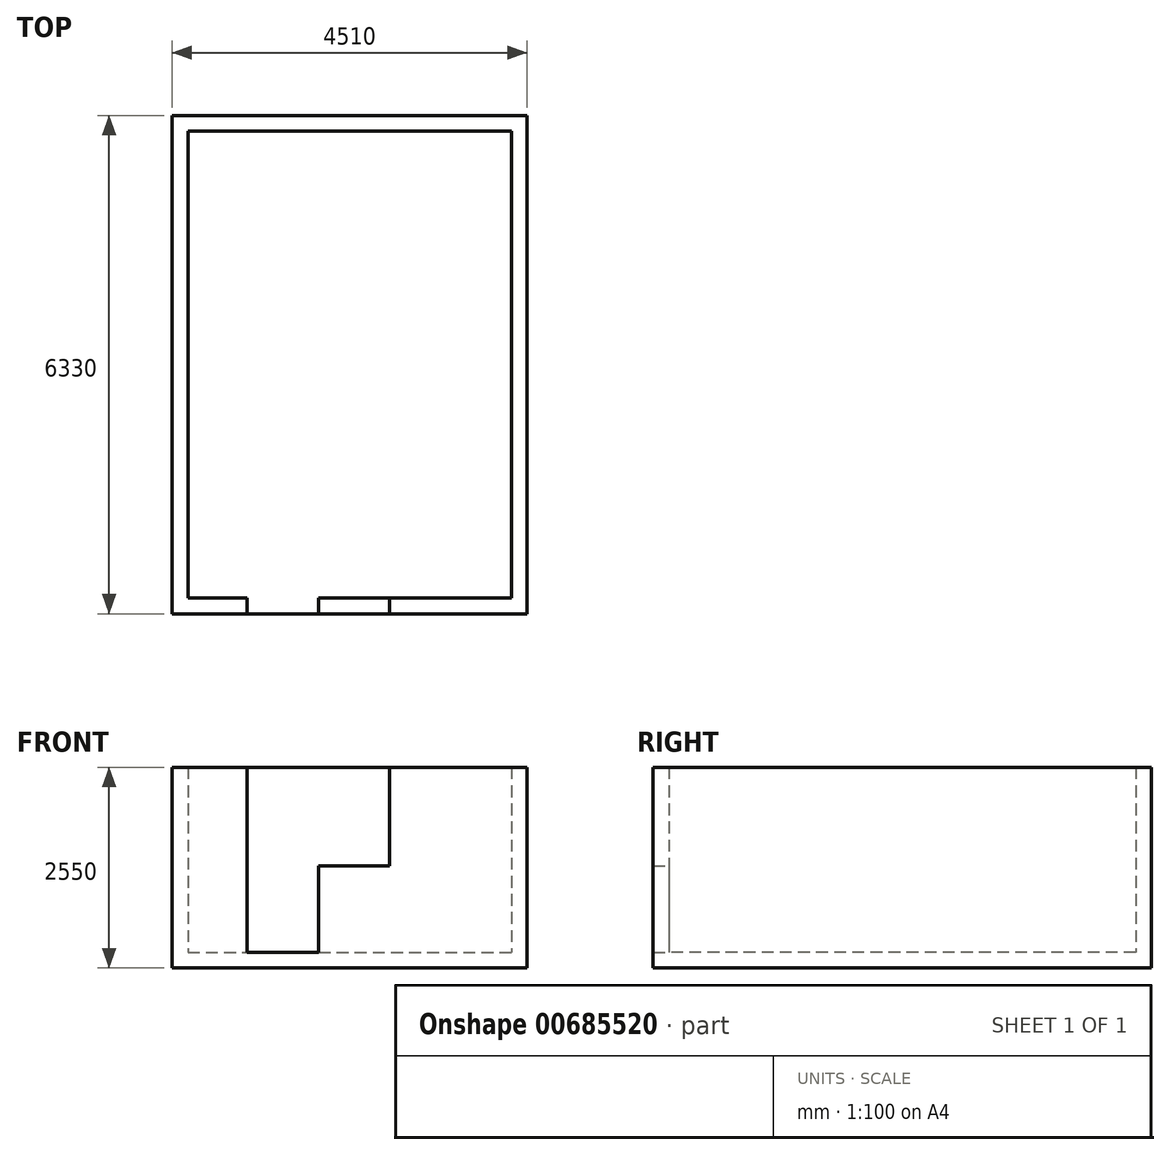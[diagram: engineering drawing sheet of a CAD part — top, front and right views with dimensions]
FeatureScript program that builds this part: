
annotation { "Feature Type Name" : "Feature", "Feature Type Description" : "" }
export const myFeature = defineFeature(function(context is Context, id is Id, definition is map)
    precondition{}
    {
        {
            var Q0;
            Q0=qCreatedBy(makeId("Top.planeOp"),FACE);
            var sketch = newSketch(context, id + "F0", { "sketchPlane" : qUnion([Q0])});
            skLineSegment(sketch, "E0.bottom", {"start": v(-2265.16, 3785.8) * mm, "end": v(2244.84, 3785.8) * mm});
            skLineSegment(sketch, "E0.top", {"start": v(-2265.16, -2544.2) * mm, "end": v(2244.84, -2544.2) * mm});
            skLineSegment(sketch, "E0.left", {"start": v(-2265.16, 3785.8) * mm, "end": v(-2265.16, -2544.2) * mm});
            skLineSegment(sketch, "E0.right", {"start": v(2244.84, 3785.8) * mm, "end": v(2244.84, -2544.2) * mm});
            skSolve(sketch);
        }
        {
            var Q0;
            Q0=makeQuery(id+"F0.imprint","IMPRINT",FACE,{"disambiguationData":[TD([[makeQuery(id+"F0.imprint","IMPRINT",EDGE,{"derivedFrom":sQuery(id+"F0.wireOp",EDGE,"E0.bottom")}),-1.0]])]});
            extrude(context, id + "F1", {"entities" : qUnion([Q0]), "depth" : 200 * mm, "offsetDistance" : 25 * mm});
        }
        {
            var Q0;
            Q0=makeQuery(id+"F1.opExtrude","CAP_FACE",FACE,{"disambiguationData":[OSD([sQuery(id+"F0.wireOp",EDGE,"E0.bottom"),sQuery(id+"F0.wireOp",EDGE,"E0.top"),sQuery(id+"F0.wireOp",EDGE,"E0.left"),sQuery(id+"F0.wireOp",EDGE,"E0.right")])],"isStart":false});
            var sketch = newSketch(context, id + "F2", { "sketchPlane" : qUnion([Q0])});
            skLineSegment(sketch, "E1.bottom", {"start": v(-2065.16, 3585.8) * mm, "end": v(2044.84, 3585.8) * mm});
            skLineSegment(sketch, "E1.top", {"start": v(-2065.16, -2344.2) * mm, "end": v(2044.84, -2344.2) * mm});
            skLineSegment(sketch, "E1.left", {"start": v(-2065.16, 3585.8) * mm, "end": v(-2065.16, -2344.2) * mm});
            skLineSegment(sketch, "E1.right", {"start": v(2044.84, 3585.8) * mm, "end": v(2044.84, -2344.2) * mm});
            skLineSegment(sketch, "E2.bottom", {"start": v(-2265.16, 3785.8) * mm, "end": v(2244.84, 3785.8) * mm});
            skLineSegment(sketch, "E2.top", {"start": v(-2265.16, -2544.2) * mm, "end": v(2244.84, -2544.2) * mm});
            skLineSegment(sketch, "E2.left", {"start": v(-2265.16, 3785.8) * mm, "end": v(-2265.16, -2544.2) * mm});
            skLineSegment(sketch, "E2.right", {"start": v(2244.84, 3785.8) * mm, "end": v(2244.84, -2544.2) * mm});
            skSolve(sketch);
        }
        {
            var Q0;
            Q0=makeQuery(id+"F2.imprint","IMPRINT",FACE,{"disambiguationData":[TD([[makeQuery(id+"F2.imprint","IMPRINT",EDGE,{"derivedFrom":sQuery(id+"F2.wireOp",EDGE,"E1.bottom")}),1.0]])]});
            extrude(context, id + "F3", {"entities" : qUnion([Q0]), "operationType" : NewBodyOperationType.ADD, "depth" : 2350 * mm, "offsetDistance" : 25 * mm});
        }
        {
            var Q0;
            Q0=makeQuery(id+"F3.opExtrude","SWEPT_FACE",FACE,{"disambiguationData":[OSD([sQuery(id+"F2.wireOp",EDGE,"E1.top")])]});
            var sketch = newSketch(context, id + "F4", { "sketchPlane" : qUnion([Q0])});
            skLineSegment(sketch, "E3.bottom", {"start": v(-494.84, 2550) * mm, "end": v(405.16, 2550) * mm});
            skLineSegment(sketch, "E3.top", {"start": v(-494.84, 1300) * mm, "end": v(405.16, 1300) * mm});
            skLineSegment(sketch, "E3.left", {"start": v(-494.84, 2550) * mm, "end": v(-494.84, 1300) * mm});
            skLineSegment(sketch, "E4", {"start": v(405.16, 1300) * mm, "end": v(405.16, 200) * mm});
            skLineSegment(sketch, "E5", {"start": v(405.16, 200) * mm, "end": v(1315.16, 200) * mm});
            skLineSegment(sketch, "E6", {"start": v(1315.16, 200) * mm, "end": v(1315.16, 2550) * mm});
            skLineSegment(sketch, "E7", {"start": v(1315.16, 2550) * mm, "end": v(405.16, 2550) * mm});
            skSolve(sketch);
        }
        {
            var Q0;
            Q0=makeQuery(id+"F4.imprint","IMPRINT",FACE,{"disambiguationData":[TD([[makeQuery(id+"F4.imprint","IMPRINT",EDGE,{"derivedFrom":sQuery(id+"F4.wireOp",EDGE,"E3.bottom")}),1.0]])]});
            var Q1;
            Q1=makeQuery(id+"F3.boolean.opBoolean","MERGE",FACE,{"derivedFrom":[makeQuery(id+"F1.opExtrude","SWEPT_FACE",FACE,{"disambiguationData":[OSD([sQuery(id+"F0.wireOp",EDGE,"E0.top")])]}),makeQuery(id+"F3.opExtrude","SWEPT_FACE",FACE,{"disambiguationData":[OSD([sQuery(id+"F2.wireOp",EDGE,"E2.top")])]})]});
            extrude(context, id + "F5", {"entities" : qUnion([Q0]), "operationType" : NewBodyOperationType.REMOVE, "endBound" : BoundingType.UP_TO_SURFACE, "oppositeDirection" : true, "depth" : 25 * mm, "endBoundEntityFace" : qUnion([Q1]), "offsetDistance" : 25 * mm});
        }
    });
